FCSTD DOCUMENT  (FreeCAD 0.15R4671 (Git))
Label: XCarrageBottom_II
License: All rights reserved
LicenseURL: http://en.wikipedia.org/wiki/All_rights_reserved
objects: Sketcher::SketchObject×35, Part::Feature×27, Mesh::Feature×26, PartDesign::Pocket×24, PartDesign::Fillet×14, PartDesign::Pad×11, Part::MultiFuse×1
note: 147 computed .brp shape members not serialized (recipe doc carries the construction recipe); baked Part::Feature solids carry a one-line shape summary decoded from their .brp

FEATURE [Part::Feature] Part__Feature  label="OB1515_45mm001"
  Placement = pos=(0,79.5,22.5) rot=(1,0,0;1.5708rad)
  shape: bbox 15 x 45 x 15 mm, 158 faces (baked)
FEATURE [Part::Feature] Part__Feature001  label="OB1515_45mm"
  Placement = pos=(7,93,-15) rot=(0,0,1;0.785398rad)
  shape: bbox 21.01 x 21.01 x 45 mm, 158 faces (baked)
FEATURE [Part::Feature] Part__Feature002  label="OB1515_45mm002"
  Placement = pos=(20.5,100,22.5) rot=(0.57735,0.57735,0.57735;2.0944rad)
  shape: bbox 45 x 15 x 15 mm, 158 faces (baked)
FEATURE [Part::Feature] Part__Feature003  label="NEMA17"
  Placement = pos=(36,64,2) rot=(0,0,1;0rad)
  shape: bbox 42.3 x 42.3 x 68 mm, 275 faces (baked)
FEATURE [Part::Feature] Part__Feature004  label="T5_Pulley"
  Placement = pos=(36,64,-4) rot=(0,0,1;0rad)
  shape: bbox 16 x 16 x 14.8 mm, 116 faces (baked)
FEATURE [Mesh::Feature] _08ZZ_Ball_Bearing  label="608ZZ_Ball_Bearing001"
  Placement = pos=(54.5,64,25.1) rot=(0,0,1;0rad)
FEATURE [Mesh::Feature] Spacer
  Placement = pos=(21.5,54,17.6) rot=(0,0,1;0rad)
FEATURE [Mesh::Feature] _mmRod_x100mm  label="8mmRod_x100mm"
  Placement = pos=(36,-64.5,-3.5) rot=(0,0,1;3.14159rad)
FEATURE [Part::Feature] Part__Feature005  label="TopCornerMotor"
  Placement = pos=(0,100,0) rot=(0,0,1;0rad)
  shape: bbox 69.55 x 77 x 28 mm, 82 faces (baked)
FEATURE [Part::Feature] Part__Feature006  label="TopRodHolder"
  Placement = pos=(0,100,2) rot=(0,0,1;0rad)
  shape: bbox 30.16 x 11.33 x 11.99 mm, 58 faces (baked)
FEATURE [Part::Feature] LM8UU_8mm_Linear_Bearing001
  Placement = pos=(36,-24.5,-3.5) rot=(0,0,1;1.5708rad)
  shape: bbox 15 x 24 x 15 mm, 34 faces (baked)
FEATURE [Mesh::Feature] _mmRod_x100mm001  label="8mmRod_x100mm001"
  Placement = pos=(45,7.5,1.5) rot=(0,0,1;1.5708rad)
FEATURE [Mesh::Feature] _mmRod_x100mm002  label="8mmRod_x100mm002"
  Placement = pos=(45,-32.5,1.5) rot=(0,0,1;1.5708rad)
FEATURE [Mesh::Feature] _0mmFan  label="40mmFan"
  Placement = pos=(102,-18,-36) rot=(-1,0,0;1.5708rad)
FEATURE [Mesh::Feature] HexHotEnd  label="HexHotEnd1"
  Placement = pos=(104,-57,-34) rot=(0,0,1;0rad)
FEATURE [Mesh::Feature] PNEUMATIC_NIPPLE
  Placement = pos=(111,-50,-28) rot=(0,-1,0;1.5708rad)
FEATURE [Part::Feature] Part__Feature015  label="AluAngle"
  Placement = pos=(0,5,-80) rot=(-1,0,0;1.5708rad)
  shape: bbox 50 x 50.8 x 50.8 mm, 9 faces (baked)
FEATURE [Mesh::Feature] _x10x4_FlangedBearing  label="5x10x4_FlangedBearing_BOTTOM"
  Placement = pos=(49,-6,16) rot=(-1,0,0;1.5708rad)
FEATURE [Mesh::Feature] _x10x4_FlangedBearing001  label="5x10x4_FlangedBearing_TOP"
  Placement = pos=(49,-6,12) rot=(1,0,0;1.5708rad)
FEATURE [Mesh::Feature] _x10x4_FlangedBearing002  label="5x10x4_FlangedBearing_BOTTOM001"
  Placement = pos=(49,-19,16) rot=(-1,0,0;1.5708rad)
FEATURE [Mesh::Feature] _x10x4_FlangedBearing003  label="5x10x4_FlangedBearing_TOP001"
  Placement = pos=(49,-19,12) rot=(1,0,0;1.5708rad)
FEATURE [Part::Feature] Part__Feature016  label="XCarrageBeltBlock"
  Placement = pos=(9,0,0) rot=(0,0,1;0rad)
  shape: bbox 56 x 22 x 10 mm, 113 faces (baked)
FEATURE [Part::Feature] Part__Feature017  label="LJ18A3"
  Placement = pos=(136,-57,-52) rot=(0,0,1;0rad)
  shape: bbox 17.85 x 17.85 x 79.1 mm, 11 faces (baked)
FEATURE [Mesh::Feature] HexNutStyle1_M002  label="HexNutStyle1_M006"
  Placement = pos=(50.3,7.15,-114) rot=(0,0,1;0.523599rad)
FEATURE [Mesh::Feature] HexNutStyle1_M003  label="HexNutStyle1_M007"
  Placement = pos=(50.3,20.15,-114) rot=(0,0,1;0.523599rad)
FEATURE [Part::Feature] Part__Feature018  label="YCarrage"
  shape: bbox 34.23 x 25.99 x 62.01 mm, 85 faces (baked)
FEATURE [Part::Feature] LM8UU_8mm_Linear_Bearing
  Placement = pos=(95,7.5,1.5) rot=(-1,0,0;1.5708rad)
  shape: bbox 24 x 15 x 15 mm, 34 faces (baked)
FEATURE [Part::Feature] LM8UU_8mm_Linear_Bearing002
  Placement = pos=(95,-32.5,1.5) rot=(-1,0,0;1.5708rad)
  shape: bbox 24 x 15 x 15 mm, 34 faces (baked)
FEATURE [Part::Feature] LM8UU_8mm_Linear_Bearing003
  Placement = pos=(123,7.5,1.5) rot=(-1,0,0;1.5708rad)
  shape: bbox 24 x 15 x 15 mm, 34 faces (baked)
FEATURE [Part::Feature] LM8UU_8mm_Linear_Bearing004
  Placement = pos=(123,-32.5,1.5) rot=(-1,0,0;1.5708rad)
  shape: bbox 24 x 15 x 15 mm, 34 faces (baked)
FEATURE [Mesh::Feature] MicroSwitch
  Placement = pos=(99,-12.5,-5) rot=(0,0,1;1.5708rad)
FEATURE [Sketcher::SketchObject] Sketch
  Placement = pos=(0,0,-10) rot=(0,0,1;0rad)
  sketch-geometry (4):
    g0: LineSegment StartX=93 StartY=18 StartZ=0 EndX=149 EndY=18 EndZ=0
    g1: LineSegment StartX=149 StartY=18 StartZ=0 EndX=149 EndY=-70 EndZ=0
    g2: LineSegment StartX=149 StartY=-70 StartZ=0 EndX=93 EndY=-70 EndZ=0
    g3: LineSegment StartX=93 StartY=-70 StartZ=0 EndX=93 EndY=18 EndZ=0
  constraints (8):
    c: Coincident(g0,g1)
    c: Coincident(g1,g2)
    c: Coincident(g2,g3)
    c: Coincident(g3,g0)
    c: Horizontal(g0)
    c: Horizontal(g2)
    c: Vertical(g1)
    c: Vertical(g3)
FEATURE [PartDesign::Pad] Pad
  Length = 11.5
  Length2 = 100
  Placement = pos=(0,0,-10) rot=(0,0,1;0rad)
  Sketch = -> Sketch
  Type = 0
FEATURE [Sketcher::SketchObject] Sketch001
  Placement = pos=(149,0,-10) rot=(0.57735,0.57735,0.57735;2.0944rad)
  Support = -> Pad [Face2]
  sketch-geometry (2):
    g0: Circle CenterX=-32.5 CenterY=11.5 CenterZ=0 NormalX=0 NormalY=0 NormalZ=1 Radius=7.75
    g1: Circle CenterX=7.5 CenterY=11.5 CenterZ=0 NormalX=0 NormalY=0 NormalZ=1 Radius=7.75
  constraints (2):
    c: Radius(g0) = 7.75
    c: Radius(g1) = 7.75
FEATURE [PartDesign::Pocket] Pocket
  Length = 26.25
  Placement = pos=(0,0,-10) rot=(0,0,1;0rad)
  Sketch = -> Sketch001
  Type = 0
FEATURE [Sketcher::SketchObject] Sketch002
  Placement = pos=(93,0,-10) rot=(0.57735,-0.57735,-0.57735;2.0944rad)
  Support = -> Pocket [Face2]
  sketch-geometry (2):
    g0: Circle CenterX=-7.5 CenterY=11.5 CenterZ=0 NormalX=0 NormalY=0 NormalZ=1 Radius=7.5
    g1: Circle CenterX=32.5 CenterY=11.5 CenterZ=0 NormalX=0 NormalY=0 NormalZ=1 Radius=7.75
  constraints (2):
    c: Radius(g1) = 7.75
    c: Radius(g0) = 7.5
FEATURE [PartDesign::Pocket] Pocket001
  Length = 26.25
  Placement = pos=(0,0,-10) rot=(0,0,1;0rad)
  Sketch = -> Sketch002
  Type = 0
FEATURE [Sketcher::SketchObject] Sketch003
  Placement = pos=(149,0,-10) rot=(0.57735,0.57735,0.57735;2.0944rad)
  Support = -> Pocket001 [Face3]
  sketch-geometry (4):
    g0: LineSegment StartX=-41 StartY=11.5 StartZ=0 EndX=15.5 EndY=11.5 EndZ=0
    g1: LineSegment StartX=15.5 StartY=11.5 StartZ=0 EndX=15.5 EndY=3 EndZ=0
    g2: LineSegment StartX=15.5 StartY=3 StartZ=0 EndX=-41 EndY=3 EndZ=0
    g3: LineSegment StartX=-41 StartY=3 StartZ=0 EndX=-41 EndY=11.5 EndZ=0
  constraints (8):
    c: Coincident(g0,g1)
    c: Coincident(g1,g2)
    c: Coincident(g2,g3)
    c: Coincident(g3,g0)
    c: Horizontal(g0)
    c: Horizontal(g2)
    c: Vertical(g1)
    c: Vertical(g3)
FEATURE [PartDesign::Pad] Pad001
  Length = 1.25
  Length2 = 100
  Placement = pos=(0,0,-10) rot=(0,0,1;0rad)
  Reversed = true
  Sketch = -> Sketch003
  Type = 0
FEATURE [Sketcher::SketchObject] Sketch004
  Placement = pos=(93,0,-10) rot=(0.57735,-0.57735,-0.57735;2.0944rad)
  Support = -> Pad001 [Face2]
  sketch-geometry (4):
    g0: LineSegment StartX=-15.5 StartY=11.5 StartZ=0 EndX=41 EndY=11.5 EndZ=0
    g1: LineSegment StartX=41 StartY=11.5 StartZ=0 EndX=41 EndY=3 EndZ=0
    g2: LineSegment StartX=41 StartY=3 StartZ=0 EndX=-15.5 EndY=3 EndZ=0
    g3: LineSegment StartX=-15.5 StartY=3 StartZ=0 EndX=-15.5 EndY=11.5 EndZ=0
  constraints (8):
    c: Coincident(g0,g1)
    c: Coincident(g1,g2)
    c: Coincident(g2,g3)
    c: Coincident(g3,g0)
    c: Horizontal(g0)
    c: Horizontal(g2)
    c: Vertical(g1)
    c: Vertical(g3)
FEATURE [PartDesign::Pad] Pad002
  Length = 1.25
  Length2 = 100
  Placement = pos=(0,0,-10) rot=(0,0,1;0rad)
  Reversed = true
  Sketch = -> Sketch004
  Type = 0
FEATURE [Sketcher::SketchObject] Sketch005
  Placement = pos=(149,0,-10) rot=(0.57735,0.57735,0.57735;2.0944rad)
  Support = -> Pad002 [Face2]
  sketch-geometry (2):
    g0: Circle CenterX=-32.5 CenterY=11.5 CenterZ=0 NormalX=0 NormalY=0 NormalZ=1 Radius=6
    g1: Circle CenterX=7.5 CenterY=11.5 CenterZ=0 NormalX=0 NormalY=0 NormalZ=1 Radius=6
  constraints (2):
    c: Radius(g0) = 6
    c: Radius(g1) = 6
FEATURE [PartDesign::Pocket] Pocket002
  Length = 5
  Placement = pos=(0,0,-10) rot=(0,0,1;0rad)
  Sketch = -> Sketch005
  Type = 1
FEATURE [Part::Feature] Pocket003
  shape: bbox 56 x 88 x 11.5 mm, 26 faces (baked)
FEATURE [Sketcher::SketchObject] Sketch006
  Placement = pos=(0,0,1.5) rot=(0,0,1;0rad)
  Support = -> Pocket003 [Face7]
  sketch-geometry (8):
    g0: LineSegment StartX=93.75 StartY=-2.25 StartZ=0 EndX=145.5 EndY=-2.25 EndZ=0
    g1: LineSegment StartX=145.5 StartY=-2.25 StartZ=0 EndX=145.5 EndY=-22.75 EndZ=0
    g2: LineSegment StartX=145.5 StartY=-22.75 StartZ=0 EndX=93.75 EndY=-22.75 EndZ=0
    g3: LineSegment StartX=93.75 StartY=-22.75 StartZ=0 EndX=93.75 EndY=-22 EndZ=0
    g4: LineSegment StartX=93.75 StartY=-22 StartZ=0 EndX=92.5 EndY=-22 EndZ=0
    g5: LineSegment StartX=92.5 StartY=-22 StartZ=0 EndX=92.5 EndY=-3 EndZ=0
    g6: LineSegment StartX=92.5 StartY=-3 StartZ=0 EndX=93.75 EndY=-3 EndZ=0
    g7: LineSegment StartX=93.75 StartY=-3 StartZ=0 EndX=93.75 EndY=-2.25 EndZ=0
  constraints (9):
    c: Coincident(g0,g1)
    c: Coincident(g1,g2)
    c: Horizontal(g0)
    c: Horizontal(g2)
    c: Vertical(g1)
    c: Coincident(g3,g4)
    c: Coincident(g4,g5)
    c: Coincident(g5,g6)
    c: Coincident(g6,g7)
FEATURE [PartDesign::Pocket] Pocket004
  Length = 7
  Sketch = -> Sketch006
  Type = 0
FEATURE [Sketcher::SketchObject] Sketch007
  Placement = pos=(0,0,1.5) rot=(0,0,1;0rad)
  Support = -> Pocket004 [Face12]
  sketch-geometry (2):
    g0: Circle CenterX=104 CenterY=-57.0828 CenterZ=0 NormalX=0 NormalY=0 NormalZ=1 Radius=8.1
    g1: Circle CenterX=136 CenterY=-57 CenterZ=0 NormalX=0 NormalY=0 NormalZ=1 Radius=9.1
  constraints (2):
    c: Radius(g1) = 9.1
    c: Radius(g0) = 8.1
FEATURE [PartDesign::Pocket] Pocket005
  Length = 5
  Sketch = -> Sketch007
  Type = 1
FEATURE [Sketcher::SketchObject] Sketch008
  Placement = pos=(0,-70,0) rot=(1,0,0;1.5708rad)
  Support = -> Pocket005 [Face13]
  sketch-geometry (2):
    g0: Circle CenterX=111.593 CenterY=-4.65129 CenterZ=0 NormalX=0 NormalY=0 NormalZ=1 Radius=1.65
    g1: Circle CenterX=96.4021 CenterY=-4.66548 CenterZ=0 NormalX=0 NormalY=0 NormalZ=1 Radius=1.65
  constraints (2):
    c: Radius(g1) = 1.65
    c: Radius(g0) = 1.65
FEATURE [PartDesign::Pocket] Pocket006
  Length = 25
  Sketch = -> Sketch008
  Type = 0
FEATURE [PartDesign::Fillet] Fillet
  Base = -> Pocket006 [Edge1,Edge2]
  Radius = 2
FEATURE [PartDesign::Fillet] Fillet001
  Base = -> Fillet [Edge31,Edge44]
  Radius = 2
FEATURE [Sketcher::SketchObject] Sketch009
  Placement = pos=(0,0,1.5) rot=(0,0,1;0rad)
  Support = -> Fillet001 [Face15]
  sketch-geometry (1):
    g0: Circle CenterX=104 CenterY=-57 CenterZ=0 NormalX=0 NormalY=0 NormalZ=1 Radius=10
  constraints (1):
    c: Radius(g0) = 10
FEATURE [PartDesign::Pad] Pad003
  Length = 5
  Length2 = 100
  Sketch = -> Sketch009
  Type = 0
FEATURE [PartDesign::Fillet] Fillet002
  Base = -> Pad003 [Edge2,Edge1]
  Radius = 1
FEATURE [Sketcher::SketchObject] Sketch010
  Placement = pos=(0,0,6.5) rot=(0,0,1;0rad)
  Support = -> Fillet002 [Face1]
  sketch-geometry (1):
    g0: Circle CenterX=104 CenterY=-57 CenterZ=0 NormalX=0 NormalY=0 NormalZ=1 Radius=4.75
  constraints (1):
    c: Radius(g0) = 4.75
FEATURE [PartDesign::Pocket] Pocket007
  Length = 6
  Sketch = -> Sketch010
  Type = 0
FEATURE [Sketcher::SketchObject] Sketch011
  Placement = pos=(0,0,-5.5) rot=(0,0,1;0rad)
  Support = -> Pocket007 [Face38]
  sketch-geometry (4):
    g0: LineSegment StartX=145.5 StartY=-2.25 StartZ=0 EndX=129.5 EndY=-2.25 EndZ=0
    g1: LineSegment StartX=129.5 StartY=-2.25 StartZ=0 EndX=129.5 EndY=-22.75 EndZ=0
    g2: LineSegment StartX=129.5 StartY=-22.75 StartZ=0 EndX=145.5 EndY=-22.75 EndZ=0
    g3: LineSegment StartX=145.5 StartY=-22.75 StartZ=0 EndX=145.5 EndY=-2.25 EndZ=0
  constraints (8):
    c: Coincident(g0,g1)
    c: Coincident(g1,g2)
    c: Coincident(g2,g3)
    c: Coincident(g3,g0)
    c: Horizontal(g0)
    c: Horizontal(g2)
    c: Vertical(g1)
    c: Vertical(g3)
FEATURE [PartDesign::Pocket] Pocket008
  Length = 5
  Sketch = -> Sketch011
  Type = 0
FEATURE [Part::Feature] Pocket009
  shape: bbox 57.67 x 88 x 16.5 mm, 53 faces (baked)
FEATURE [PartDesign::Fillet] Fillet003
  Base = -> Pocket009 [Edge164,Edge165,Edge162,Edge163]
  Radius = 4
FEATURE [PartDesign::Fillet] Fillet004
  Base = -> Fillet003 [Edge25]
  Radius = 3
FEATURE [Part::Feature] Part__Feature019  label="XCarrageTop"
  shape: bbox 56 x 70.62 x 16.52 mm, 278 faces (baked)
FEATURE [Part::Feature] Part__Feature020  label="ChinaBlowerFan"
  shape: bbox 33.55 x 33.55 x 13 mm, 169 faces (baked)
FEATURE [Part::Feature] Part__Feature021  label="ChinaBlowerFan001"
  shape: bbox 40.62 x 40.6 x 19.6 mm, 81 faces (baked)
FEATURE [Part::MultiFuse] Fusion  label="ChinaBlowerFan002"
  Placement = pos=(114,-4,-13) rot=(0.707107,0.707107,0;3.14159rad)
  Shapes = -> [Part__Feature020,Part__Feature021]
FEATURE [Mesh::Feature] _0mmFan001  label="40mmFan001"
FEATURE [Mesh::Feature] ALIEXPRESS_Aluhotend40mmFan
FEATURE [Mesh::Feature] Fan_25mm_x_10mm
  Placement = pos=(105.5,-31,-23) rot=(0,0.707107,0.707107;3.14159rad)
FEATURE [Mesh::Feature] HexHotEnd2
  Placement = pos=(104,-57,-34) rot=(0,0,1;0rad)
FEATURE [Part::Feature] Part__Feature022  label="Hexagon fanshroud"
  shape: bbox 25.5 x 25.5 x 18 mm, 35 faces (baked)
FEATURE [Mesh::Feature] hexagon_fan
  Placement = pos=(198.15,-46.7,56) rot=(0.57735,-0.57735,0.57735;2.0944rad)
FEATURE [Part::Feature] Part__Feature023  label="HexagonHotendFanShroud"
  shape: bbox 25.53 x 43.75 x 27.5 mm, 64 faces (baked)
FEATURE [Mesh::Feature] Fan_25mm_x_10mm001
  Placement = pos=(105.5,-31,-25.5) rot=(0,0.707107,0.707107;3.14159rad)
FEATURE [Sketcher::SketchObject] Sketch012
  Placement = pos=(0,0,-10) rot=(1,0,0;3.14159rad)
  Support = -> Fillet004 [Face4]
  sketch-geometry (1):
    g0: Circle CenterX=121 CenterY=12.5 CenterZ=0 NormalX=0 NormalY=0 NormalZ=1 Radius=6.5
FEATURE [PartDesign::Pad] Pad004
  Length = 11.5
  Length2 = 100
  Reversed = true
  Sketch = -> Sketch012
  Type = 0
FEATURE [Sketcher::SketchObject] Sketch013
  Placement = pos=(0,0,-10) rot=(1,0,0;3.14159rad)
  Support = -> Pad004 [Face56]
  sketch-geometry (1):
    g0: Circle CenterX=121 CenterY=12.5 CenterZ=0 NormalX=0 NormalY=0 NormalZ=1 Radius=1.8
  constraints (1):
    c: Radius(g0) = 1.8
FEATURE [PartDesign::Pocket] Pocket010
  Length = 5
  Sketch = -> Sketch013
  Type = 1
FEATURE [Sketcher::SketchObject] Sketch014
  Placement = pos=(0,0,-10) rot=(1,0,0;3.14159rad)
  Support = -> Pocket010 [Face6]
  sketch-geometry (1):
    g0: Circle CenterX=121 CenterY=12.5 CenterZ=0 NormalX=0 NormalY=0 NormalZ=1 Radius=3.6
  constraints (1):
    c: Radius(g0) = 3.6
FEATURE [PartDesign::Pocket] Pocket011
  Length = 9.5
  Sketch = -> Sketch014
  Type = 0
FEATURE [PartDesign::Fillet] Fillet005
  Base = -> Pocket011 [Edge4]
  Radius = 2
FEATURE [PartDesign::Fillet] Fillet006
  Base = -> Fillet005 [Edge3]
  Radius = 1
FEATURE [Sketcher::SketchObject] Sketch015
  Placement = pos=(0,0,-10) rot=(1,0,0;3.14159rad)
  Support = -> Fillet006 [Face19]
  sketch-geometry (4):
    g0: ArcOfCircle CenterX=121 CenterY=-18 CenterZ=0 NormalX=0 NormalY=0 NormalZ=1 Radius=4 StartAngle=3.14159 EndAngle=6.28319
    g1: LineSegment StartX=117 StartY=-18 StartZ=0 EndX=117 EndY=-17.5 EndZ=0
    g2: LineSegment StartX=117 StartY=-17.5 StartZ=0 EndX=125 EndY=-17.5 EndZ=0
    g3: LineSegment StartX=125 StartY=-17.5 StartZ=0 EndX=125 EndY=-18 EndZ=0
  constraints (7):
    c: Tangent(g0,g1) = 1.5708
    c: Coincident(g1,g2)
    c: Horizontal(g2)
    c: Coincident(g2,g3)
    c: Coincident(g3,g0)
    c: Vertical(g3)
    c: Tangent(g3,g0)
FEATURE [PartDesign::Pad] Pad005
  Length = 11.5
  Length2 = 100
  Reversed = true
  Sketch = -> Sketch015
  Type = 0
FEATURE [Sketcher::SketchObject] Sketch016
  Placement = pos=(0,0,-10) rot=(1,0,0;3.14159rad)
  Support = -> Pad005 [Face67]
  sketch-geometry (2):
    g0: Circle CenterX=121 CenterY=-18 CenterZ=0 NormalX=0 NormalY=0 NormalZ=1 Radius=1.8
    g1: Circle CenterX=121 CenterY=43 CenterZ=0 NormalX=0 NormalY=0 NormalZ=1 Radius=1.8
  constraints (2):
    c: Radius(g1) = 1.8
    c: Radius(g0) = 1.8
FEATURE [PartDesign::Pocket] Pocket012
  Length = 5
  Sketch = -> Sketch016
  Type = 1
FEATURE [Sketcher::SketchObject] Sketch017
  Placement = pos=(0,0,-10) rot=(1,0,0;3.14159rad)
  Support = -> Pocket012 [Face2]
  sketch-geometry (2):
    g0: Circle CenterX=121 CenterY=-18 CenterZ=0 NormalX=0 NormalY=0 NormalZ=1 Radius=3.3
    g1: Circle CenterX=121 CenterY=43 CenterZ=0 NormalX=0 NormalY=0 NormalZ=1 Radius=3.3
  constraints (2):
    c: Radius(g1) = 3.3
    c: Radius(g0) = 3.3
FEATURE [PartDesign::Pocket] Pocket013
  Length = 9.5
  Sketch = -> Sketch017
  Type = 0
FEATURE [Sketcher::SketchObject] Sketch018
  Placement = pos=(0,0,-10) rot=(1,0,0;3.14159rad)
  Support = -> Pocket013 [Face2]
  sketch-geometry (3):
    g0: Circle CenterX=114.5 CenterY=22 CenterZ=0 NormalX=0 NormalY=0 NormalZ=1 Radius=1.5
    g1: Circle CenterX=96.5 CenterY=22 CenterZ=0 NormalX=0 NormalY=0 NormalZ=1 Radius=1.5
    g2: Circle CenterX=107 CenterY=44.25 CenterZ=0 NormalX=0 NormalY=0 NormalZ=1 Radius=1.5
  constraints (3):
    c: Radius(g2) = 1.5
    c: Radius(g0) = 1.5
    c: Radius(g1) = 1.5
FEATURE [PartDesign::Pocket] Pocket014
  Length = 5
  Sketch = -> Sketch018
  Type = 0
FEATURE [Sketcher::SketchObject] Sketch019
  Placement = pos=(0,0,1.5) rot=(0,0,1;0rad)
  Support = -> Pocket014 [Face39]
  sketch-geometry (1):
    g0: Circle CenterX=121 CenterY=-53 CenterZ=0 NormalX=0 NormalY=0 NormalZ=1 Radius=5
FEATURE [PartDesign::Pocket] Pocket015
  Length = 5
  Sketch = -> Sketch019
  Type = 1
FEATURE [Mesh::Feature] PNEUMATIC_NIPPLE001
  Placement = pos=(111,-66,-3) rot=(0,-1,0;1.5708rad)
FEATURE [Sketcher::SketchObject] Sketch020
  Placement = pos=(0,0,-10) rot=(1,0,0;3.14159rad)
  Support = -> Pocket015 [Face2]
  sketch-geometry (12):
    g0: Circle CenterX=96 CenterY=-15 CenterZ=0 NormalX=0 NormalY=0 NormalZ=1 Radius=1.5
    g1: Circle CenterX=146 CenterY=-15 CenterZ=0 NormalX=0 NormalY=0 NormalZ=1 Radius=1.5
    g2: Circle CenterX=113 CenterY=-15 CenterZ=0 NormalX=0 NormalY=0 NormalZ=1 Radius=1.5
    g3: Circle CenterX=129 CenterY=-15 CenterZ=0 NormalX=0 NormalY=0 NormalZ=1 Radius=1.5
    g4: Circle CenterX=96 CenterY=-1 CenterZ=0 NormalX=0 NormalY=0 NormalZ=1 Radius=1.5
    g5: Circle CenterX=113 CenterY=-1 CenterZ=0 NormalX=0 NormalY=0 NormalZ=1 Radius=1.5
    g6: Circle CenterX=129 CenterY=-1 CenterZ=0 NormalX=0 NormalY=0 NormalZ=1 Radius=1.5
    g7: Circle CenterX=146 CenterY=-1 CenterZ=0 NormalX=0 NormalY=0 NormalZ=1 Radius=1.5
    g8: Circle CenterX=146 CenterY=40 CenterZ=0 NormalX=0 NormalY=0 NormalZ=1 Radius=1.5
    g9: Circle CenterX=129 CenterY=40 CenterZ=0 NormalX=0 NormalY=0 NormalZ=1 Radius=1.5
    g10: Circle CenterX=146 CenterY=26 CenterZ=0 NormalX=0 NormalY=0 NormalZ=1 Radius=1.5
    g11: Circle CenterX=129 CenterY=26 CenterZ=0 NormalX=0 NormalY=0 NormalZ=1 Radius=1.5
  constraints (12):
    c: Radius(g0) = 1.5
    c: Radius(g1) = 1.5
    c: Radius(g2) = 1.5
    c: Radius(g3) = 1.5
    c: Radius(g4) = 1.5
    c: Equal(g4,g5)
    c: Equal(g4,g6)
    c: Equal(g4,g7)
    c: Equal(g4,g10)
    c: Equal(g4,g11)
    c: Equal(g4,g9)
    c: Equal(g4,g8)
FEATURE [PartDesign::Pocket] Pocket016
  Length = 5
  Sketch = -> Sketch020
  Type = 0
FEATURE [Sketcher::SketchObject] Sketch021
  Placement = pos=(0,0,1.5) rot=(0,0,1;0rad)
  Support = -> Pocket016 [Face4]
  sketch-geometry (16):
    g0: LineSegment StartX=97 StartY=11 StartZ=0 EndX=116 EndY=11 EndZ=0
    g1: LineSegment StartX=116 StartY=11 StartZ=0 EndX=116 EndY=4 EndZ=0
    g2: LineSegment StartX=116 StartY=4 StartZ=0 EndX=97 EndY=4 EndZ=0
    g3: LineSegment StartX=97 StartY=4 StartZ=0 EndX=97 EndY=11 EndZ=0
    g4: LineSegment StartX=126 StartY=11 StartZ=0 EndX=144 EndY=11 EndZ=0
    g5: LineSegment StartX=144 StartY=11 StartZ=0 EndX=144 EndY=4 EndZ=0
    g6: LineSegment StartX=144 StartY=4 StartZ=0 EndX=126 EndY=4 EndZ=0
    g7: LineSegment StartX=126 StartY=4 StartZ=0 EndX=126 EndY=11 EndZ=0
    g8: LineSegment StartX=126 StartY=-29 StartZ=0 EndX=144 EndY=-29 EndZ=0
    g9: LineSegment StartX=144 StartY=-29 StartZ=0 EndX=144 EndY=-36 EndZ=0
    g10: LineSegment StartX=144 StartY=-36 StartZ=0 EndX=126 EndY=-36 EndZ=0
    g11: LineSegment StartX=126 StartY=-36 StartZ=0 EndX=126 EndY=-29 EndZ=0
    g12: LineSegment StartX=97 StartY=-29 StartZ=0 EndX=116 EndY=-29 EndZ=0
    g13: LineSegment StartX=116 StartY=-29 StartZ=0 EndX=116 EndY=-36 EndZ=0
    g14: LineSegment StartX=116 StartY=-36 StartZ=0 EndX=97 EndY=-36 EndZ=0
    g15: LineSegment StartX=97 StartY=-36 StartZ=0 EndX=97 EndY=-29 EndZ=0
  constraints (32):
    c: Coincident(g0,g1)
    c: Coincident(g1,g2)
    c: Coincident(g2,g3)
    c: Coincident(g3,g0)
    c: Horizontal(g0)
    c: Horizontal(g2)
    c: Vertical(g1)
    c: Vertical(g3)
    c: Coincident(g4,g5)
    c: Coincident(g5,g6)
    c: Coincident(g6,g7)
    c: Coincident(g7,g4)
    c: Horizontal(g4)
    c: Horizontal(g6)
    c: Vertical(g5)
    c: Vertical(g7)
    c: Coincident(g8,g9)
    c: Coincident(g9,g10)
    c: Coincident(g10,g11)
    c: Coincident(g11,g8)
    c: Horizontal(g8)
    c: Horizontal(g10)
    c: Vertical(g9)
    c: Vertical(g11)
    c: Coincident(g12,g13)
    c: Coincident(g13,g14)
    c: Coincident(g14,g15)
    c: Coincident(g15,g12)
    c: Horizontal(g12)
    c: Horizontal(g14)
    c: Vertical(g13)
    c: Vertical(g15)
FEATURE [PartDesign::Pocket] Pocket017
  Length = 10
  Sketch = -> Sketch021
  Type = 0
FEATURE [PartDesign::Fillet] Fillet007
  Base = -> Pocket017 [Edge271,Edge261,Edge314,Edge307,Edge309,Edge264,Edge269,Edge312,Edge304,Edge317,Edge274,Edge263,Edge306,Edge315,Edge272,Edge266]
  Radius = 2
FEATURE [Part::Feature] Fillet007001  label="XCarrageBottom_x"
  shape: bbox 57.67 x 92 x 16.5 mm, 140 faces (baked)
FEATURE [Sketcher::SketchObject] Sketch022
  Placement = pos=(0,0,-5.5) rot=(0,0,1;0rad)
  Support = -> Fillet007001 [Face52]
  sketch-geometry (2):
    g0: Circle CenterX=101.75 CenterY=-7.5 CenterZ=0 NormalX=0 NormalY=0 NormalZ=1 Radius=1
    g1: Circle CenterX=101.75 CenterY=-17 CenterZ=0 NormalX=0 NormalY=0 NormalZ=1 Radius=1
  constraints (2):
    c: Radius(g0) = 1
    c: Equal(g0,g1)
FEATURE [PartDesign::Pocket] Pocket018
  Length = 5
  Sketch = -> Sketch022
  Type = 1
FEATURE [Sketcher::SketchObject] Sketch023
  Placement = pos=(0,0,-10) rot=(1,0,0;3.14159rad)
  Support = -> Pocket018 [Face47]
  sketch-geometry (4):
    g0: LineSegment StartX=94.1621 StartY=68.9384 StartZ=0 EndX=146.057 EndY=68.9384 EndZ=0
    g1: LineSegment StartX=146.057 StartY=68.9384 StartZ=0 EndX=146.057 EndY=47.25 EndZ=0
    g2: LineSegment StartX=146.057 StartY=47.25 StartZ=0 EndX=94.1621 EndY=47.25 EndZ=0
    g3: LineSegment StartX=94.1621 StartY=47.25 StartZ=0 EndX=94.1621 EndY=68.9384 EndZ=0
  constraints (8):
    c: Coincident(g0,g1)
    c: Coincident(g1,g2)
    c: Coincident(g2,g3)
    c: Coincident(g3,g0)
    c: Horizontal(g0)
    c: Horizontal(g2)
    c: Vertical(g1)
    c: Vertical(g3)
FEATURE [PartDesign::Pad] Pad006
  Length = 11.5
  Length2 = 100
  Reversed = true
  Sketch = -> Sketch023
  Type = 0
FEATURE [Sketcher::SketchObject] Sketch024
  Placement = pos=(93,0,0) rot=(0.57735,-0.57735,-0.57735;2.0944rad)
  Support = -> Pad006 [Face19]
  sketch-geometry (4):
    g0: LineSegment StartX=46 StartY=6.75 StartZ=0 EndX=72 EndY=6.75 EndZ=0
    g1: LineSegment StartX=72 StartY=6.75 StartZ=0 EndX=72 EndY=1.5 EndZ=0
    g2: LineSegment StartX=72 StartY=1.5 StartZ=0 EndX=46 EndY=1.5 EndZ=0
    g3: LineSegment StartX=46 StartY=1.5 StartZ=0 EndX=46 EndY=6.75 EndZ=0
  constraints (8):
    c: Coincident(g0,g1)
    c: Coincident(g1,g2)
    c: Coincident(g2,g3)
    c: Coincident(g3,g0)
    c: Horizontal(g0)
    c: Horizontal(g2)
    c: Vertical(g1)
    c: Vertical(g3)
FEATURE [PartDesign::Pocket] Pocket019
  Length = 24
  Sketch = -> Sketch024
  Type = 0
FEATURE [Sketcher::SketchObject] Sketch025
  Placement = pos=(0,0,1.5) rot=(0,0,1;0rad)
  Support = -> Pocket019 [Face133]
  sketch-geometry (4):
    g0: LineSegment StartX=92 StartY=-48 StartZ=0 EndX=149.731 EndY=-48 EndZ=0
    g1: LineSegment StartX=149.731 StartY=-48 StartZ=0 EndX=149.731 EndY=-72.7088 EndZ=0
    g2: LineSegment StartX=149.731 StartY=-72.7088 StartZ=0 EndX=92 EndY=-72.7088 EndZ=0
    g3: LineSegment StartX=92 StartY=-72.7088 StartZ=0 EndX=92 EndY=-48 EndZ=0
  constraints (8):
    c: Coincident(g0,g1)
    c: Coincident(g1,g2)
    c: Coincident(g2,g3)
    c: Coincident(g3,g0)
    c: Horizontal(g0)
    c: Horizontal(g2)
    c: Vertical(g1)
    c: Vertical(g3)
FEATURE [PartDesign::Pocket] Pocket020
  Length = 5
  Sketch = -> Sketch025
  Type = 1
FEATURE [Sketcher::SketchObject] Sketch026
  Placement = pos=(0,-48,0) rot=(1,0,0;1.5708rad)
  Support = -> Pocket020 [Face50]
  sketch-geometry (4):
    g0: LineSegment StartX=93 StartY=-10 StartZ=0 EndX=149 EndY=-10 EndZ=0
    g1: LineSegment StartX=149 StartY=-10 StartZ=0 EndX=149 EndY=18 EndZ=0
    g2: LineSegment StartX=149 StartY=18 StartZ=0 EndX=93 EndY=18 EndZ=0
    g3: LineSegment StartX=93 StartY=18 StartZ=0 EndX=93 EndY=-10 EndZ=0
  constraints (8):
    c: Coincident(g0,g1)
    c: Coincident(g1,g2)
    c: Coincident(g2,g3)
    c: Coincident(g3,g0)
    c: Horizontal(g0)
    c: Horizontal(g2)
    c: Vertical(g1)
    c: Vertical(g3)
FEATURE [PartDesign::Pad] Pad007
  Length = 10
  Length2 = 100
  Sketch = -> Sketch026
  Type = 0
FEATURE [PartDesign::Fillet] Fillet007002
  Base = -> Pad007 [Edge279,Edge280]
  Radius = 2
FEATURE [Sketcher::SketchObject] Sketch027
  Placement = pos=(0,0,-10) rot=(1,0,0;3.14159rad)
  Support = -> Fillet007002 [Face9]
  sketch-geometry (10):
    g0: LineSegment StartX=93 StartY=-26 StartZ=0 EndX=149 EndY=-26 EndZ=0
    g1: LineSegment StartX=149 StartY=-26 StartZ=0 EndX=149 EndY=-16 EndZ=0
    g2: LineSegment StartX=93 StartY=-16 StartZ=0 EndX=93 EndY=-26 EndZ=0
    g3: LineSegment StartX=93 StartY=-16 StartZ=0 EndX=94 EndY=-16 EndZ=0
    g4: LineSegment StartX=94 StartY=-16 StartZ=0 EndX=95 EndY=-17 EndZ=0
    g5: LineSegment StartX=95 StartY=-17 StartZ=0 EndX=117.326 EndY=-17.0688 EndZ=0
    g6: LineSegment StartX=149 StartY=-16 StartZ=0 EndX=148 EndY=-16 EndZ=0
    g7: LineSegment StartX=148 StartY=-16 StartZ=0 EndX=147 EndY=-17 EndZ=0
    g8: LineSegment StartX=147 StartY=-17 StartZ=0 EndX=124.78 EndY=-17.0424 EndZ=0
    g9: ArcOfCircle CenterX=121.056 CenterY=-17.7936 CenterZ=0 NormalX=0 NormalY=0 NormalZ=1 Radius=3.7994 StartAngle=2.94964 EndAngle=6.48221
  constraints (11):
    c: Coincident(g0,g1)
    c: Coincident(g2,g0)
    c: Horizontal(g0)
    c: Vertical(g1)
    c: Vertical(g2)
    c: Coincident(g3,g4)
    c: Coincident(g4,g5)
    c: Coincident(g6,g7)
    c: Coincident(g7,g8)
    c: Coincident(g8,g9)
    c: Coincident(g5,g9)
FEATURE [PartDesign::Pad] Pad008
  Length = 11.5
  Length2 = 100
  Reversed = true
  Sketch = -> Sketch027
  Type = 0
FEATURE [Part::Feature] Pad008001  label="Pad009"
  shape: bbox 56 x 84 x 28 mm, 131 faces (baked)
FEATURE [Sketcher::SketchObject] Sketch028
  Placement = pos=(0,26,0) rot=(0,0.707107,0.707107;3.14159rad)
  Support = -> Pad008001 [Face93]
  sketch-geometry (4):
    g0: LineSegment StartX=-138 StartY=-10 StartZ=0 EndX=-104 EndY=-10 EndZ=0
    g1: LineSegment StartX=-104 StartY=-10 StartZ=0 EndX=-104 EndY=11 EndZ=0
    g2: LineSegment StartX=-104 StartY=11 StartZ=0 EndX=-138 EndY=11 EndZ=0
    g3: LineSegment StartX=-138 StartY=11 StartZ=0 EndX=-138 EndY=-10 EndZ=0
  constraints (10):
    c: Coincident(g0,g1)
    c: Coincident(g1,g2)
    c: Coincident(g2,g3)
    c: Coincident(g3,g0)
    c: Horizontal(g0)
    c: Horizontal(g2)
    c: Vertical(g1)
    c: Vertical(g3)
    c: DistanceY(g0,g2) = 21
    c: DistanceX(g0,g0) = 34
FEATURE [PartDesign::Pad] Pad008002
  Length = 3
  Length2 = 100
  Reversed = true
  Sketch = -> Sketch028
  Type = 0
FEATURE [Sketcher::SketchObject] Sketch029
  Placement = pos=(0,0,11) rot=(0,0,1;0rad)
  Support = -> Pad008002 [Face92]
  sketch-geometry (8):
    g0: LineSegment StartX=138 StartY=24 StartZ=0 EndX=135 EndY=24 EndZ=0
    g1: LineSegment StartX=135 StartY=24 StartZ=0 EndX=135 EndY=19 EndZ=0
    g2: LineSegment StartX=135 StartY=19 StartZ=0 EndX=138 EndY=19 EndZ=0
    g3: LineSegment StartX=138 StartY=19 StartZ=0 EndX=138 EndY=24 EndZ=0
    g4: LineSegment StartX=104 StartY=24 StartZ=0 EndX=107 EndY=24 EndZ=0
    g5: LineSegment StartX=107 StartY=24 StartZ=0 EndX=107 EndY=19 EndZ=0
    g6: LineSegment StartX=107 StartY=19 StartZ=0 EndX=104 EndY=19 EndZ=0
    g7: LineSegment StartX=104 StartY=19 StartZ=0 EndX=104 EndY=24 EndZ=0
  constraints (16):
    c: Coincident(g0,g1)
    c: Coincident(g1,g2)
    c: Coincident(g2,g3)
    c: Coincident(g3,g0)
    c: Horizontal(g0)
    c: Horizontal(g2)
    c: Vertical(g1)
    c: Vertical(g3)
    c: Coincident(g4,g5)
    c: Coincident(g5,g6)
    c: Coincident(g6,g7)
    c: Coincident(g7,g4)
    c: Horizontal(g4)
    c: Horizontal(g6)
    c: Vertical(g5)
    c: Vertical(g7)
FEATURE [PartDesign::Pad] Pad008003
  Length = 10
  Length2 = 100
  Reversed = true
  Sketch = -> Sketch029
  Type = 0
FEATURE [Sketcher::SketchObject] Sketch030
  Placement = pos=(138,0,0) rot=(0.57735,0.57735,0.57735;2.0944rad)
  Support = -> Pad008003 [Face133]
  sketch-geometry (5):
    g0: LineSegment StartX=23 StartY=12 StartZ=0 EndX=23 EndY=11 EndZ=0
    g1: LineSegment StartX=23 StartY=11 StartZ=0 EndX=19 EndY=1.5 EndZ=0
    g2: LineSegment StartX=19 StartY=1.5 StartZ=0 EndX=18.5 EndY=1.5 EndZ=0
    g3: LineSegment StartX=18.5 StartY=1.5 StartZ=0 EndX=18.5 EndY=12 EndZ=0
    g4: LineSegment StartX=18.5 StartY=12 StartZ=0 EndX=23 EndY=12 EndZ=0
  constraints (5):
    c: Coincident(g0,g1)
    c: Coincident(g1,g2)
    c: Coincident(g2,g3)
    c: Coincident(g3,g4)
    c: Coincident(g4,g0)
FEATURE [PartDesign::Pocket] Pocket021
  Length = 5
  Sketch = -> Sketch030
  Type = 1
FEATURE [PartDesign::Fillet] Fillet007003
  Base = -> Pocket021 [Edge298,Edge297]
  Radius = 2
FEATURE [PartDesign::Fillet] Fillet007004
  Base = -> Fillet007003 [Edge25,Edge27]
  Radius = 2
FEATURE [PartDesign::Fillet] Fillet007005
  Base = -> Fillet007004 [Edge11,Edge21]
  Radius = 2
FEATURE [PartDesign::Fillet] Fillet007006
  Base = -> Fillet007005 [Edge79,Edge74]
  Radius = 4
FEATURE [Sketcher::SketchObject] Sketch031
  Placement = pos=(0,26,0) rot=(0,0.707107,0.707107;3.14159rad)
  Support = -> Fillet007006 [Face2]
  sketch-geometry (2):
    g0: Circle CenterX=-116.5 CenterY=0 CenterZ=0 NormalX=0 NormalY=0 NormalZ=1 Radius=1.10651
    g1: Circle CenterX=-126 CenterY=0 CenterZ=0 NormalX=0 NormalY=0 NormalZ=1 Radius=1.15631
  constraints (2):
    c: DistanceX(g1,g0) = 9.5
    c: DistanceY(g0,g1) = 0
FEATURE [PartDesign::Pocket] Pocket022
  Length = 5.5
  Sketch = -> Sketch031
  Type = 0
FEATURE [Mesh::Feature] HexNutStyle1_M3
  Placement = pos=(130.7,-95,-22) rot=(-1,0,0;1.5708rad)
FEATURE [Mesh::Feature] HexNutStyle1_M
  Placement = pos=(140.2,-95,-22) rot=(-1,0,0;1.5708rad)
FEATURE [Sketcher::SketchObject] Sketch032
  Placement = pos=(0,0,-10) rot=(1,0,0;3.14159rad)
  Support = -> Pocket022 [Face24]
  sketch-geometry (8):
    g0: LineSegment StartX=119.5 StartY=-24 StartZ=0 EndX=113.5 EndY=-24 EndZ=0
    g1: LineSegment StartX=113.5 StartY=-24 StartZ=0 EndX=113.5 EndY=-21.25 EndZ=0
    g2: LineSegment StartX=113.5 StartY=-21.25 StartZ=0 EndX=119.5 EndY=-21.25 EndZ=0
    g3: LineSegment StartX=119.5 StartY=-21.25 StartZ=0 EndX=119.5 EndY=-24 EndZ=0
    g4: LineSegment StartX=123 StartY=-21.25 StartZ=0 EndX=129 EndY=-21.25 EndZ=0
    g5: LineSegment StartX=129 StartY=-21.25 StartZ=0 EndX=129 EndY=-24 EndZ=0
    g6: LineSegment StartX=129 StartY=-24 StartZ=0 EndX=123 EndY=-24 EndZ=0
    g7: LineSegment StartX=123 StartY=-24 StartZ=0 EndX=123 EndY=-21.25 EndZ=0
  constraints (16):
    c: Coincident(g0,g1)
    c: Coincident(g1,g2)
    c: Coincident(g2,g3)
    c: Coincident(g3,g0)
    c: Horizontal(g0)
    c: Horizontal(g2)
    c: Vertical(g1)
    c: Vertical(g3)
    c: Coincident(g4,g5)
    c: Coincident(g5,g6)
    c: Coincident(g6,g7)
    c: Coincident(g7,g4)
    c: Horizontal(g4)
    c: Horizontal(g6)
    c: Vertical(g5)
    c: Vertical(g7)
FEATURE [PartDesign::Pocket] Pocket023
  Length = 13.5
  Sketch = -> Sketch032
  Type = 0
FEATURE [Part::Feature] Part__Feature024  label="HEMOUNT"
  shape: bbox 75 x 33 x 28 mm, 35 faces (baked)
FEATURE [Sketcher::SketchObject] Sketch033
  Placement = pos=(0,-58,0) rot=(1,0,0;1.5708rad)
  Support = -> Pocket023 [Face46]
  sketch-geometry (2):
    g0: Circle CenterX=107 CenterY=1 CenterZ=0 NormalX=0 NormalY=0 NormalZ=1 Radius=1.8
    g1: Circle CenterX=132 CenterY=1 CenterZ=0 NormalX=0 NormalY=0 NormalZ=1 Radius=1.8
  constraints (2):
    c: Radius(g1) = 1.8
    c: Equal(g1,g0)
FEATURE [PartDesign::Pocket] Pocket024  label="Pocket025"
  Length = 8
  Sketch = -> Sketch033
  Type = 0
FEATURE [Mesh::Feature] HexNutStyle1_M004
  Placement = pos=(146.2,-173,-21) rot=(-1,0,0;1.5708rad)
FEATURE [Mesh::Feature] HexNutStyle1_M005
  Placement = pos=(121.2,-173,-21) rot=(-1,0,0;1.5708rad)
FEATURE [Sketcher::SketchObject] Sketch034
  Placement = pos=(0,0,-10) rot=(1,0,0;3.14159rad)
  Support = -> Pocket024 [Face32]
  sketch-geometry (8):
    g0: LineSegment StartX=104 StartY=56.5 StartZ=0 EndX=110 EndY=56.5 EndZ=0
    g1: LineSegment StartX=110 StartY=56.5 StartZ=0 EndX=110 EndY=53.75 EndZ=0
    g2: LineSegment StartX=110 StartY=53.75 StartZ=0 EndX=104 EndY=53.75 EndZ=0
    g3: LineSegment StartX=104 StartY=53.75 StartZ=0 EndX=104 EndY=56.5 EndZ=0
    g4: LineSegment StartX=129 StartY=56.5 StartZ=0 EndX=135 EndY=56.5 EndZ=0
    g5: LineSegment StartX=135 StartY=56.5 StartZ=0 EndX=135 EndY=53.75 EndZ=0
    g6: LineSegment StartX=135 StartY=53.75 StartZ=0 EndX=129 EndY=53.75 EndZ=0
    g7: LineSegment StartX=129 StartY=53.75 StartZ=0 EndX=129 EndY=56.5 EndZ=0
  constraints (16):
    c: Coincident(g0,g1)
    c: Coincident(g1,g2)
    c: Coincident(g2,g3)
    c: Coincident(g3,g0)
    c: Horizontal(g0)
    c: Horizontal(g2)
    c: Vertical(g1)
    c: Vertical(g3)
    c: Coincident(g4,g5)
    c: Coincident(g5,g6)
    c: Coincident(g6,g7)
    c: Coincident(g7,g4)
    c: Horizontal(g4)
    c: Horizontal(g6)
    c: Vertical(g5)
    c: Vertical(g7)
FEATURE [PartDesign::Pocket] Pocket025  label="Pocket026"
  Length = 14.5
  Sketch = -> Sketch034
  Type = 0
FEATURE [PartDesign::Fillet] Fillet007007
  Base = -> Pocket025 [Edge254]
  Radius = 1
FEATURE [Part::Feature] Fillet007008  label="XCarrageBottom"
  shape: bbox 56.33 x 84 x 28.16 mm, 184 faces (baked)
